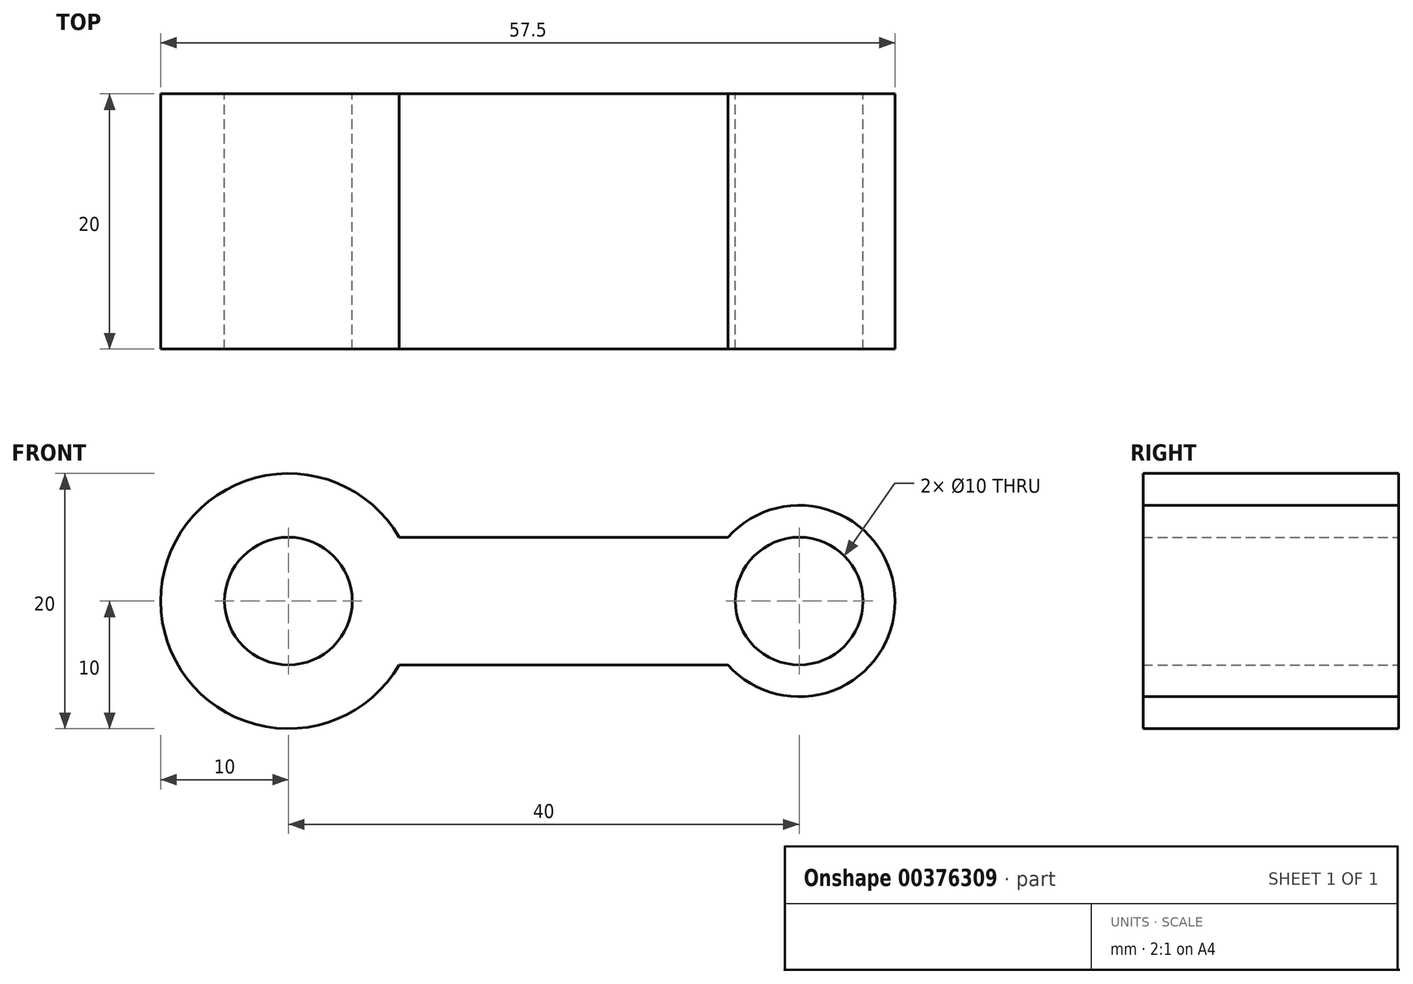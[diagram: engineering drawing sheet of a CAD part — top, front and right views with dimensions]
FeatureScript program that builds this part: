
annotation { "Feature Type Name" : "Feature", "Feature Type Description" : "" }
export const myFeature = defineFeature(function(context is Context, id is Id, definition is map)
    precondition{}
    {
        {
            var Q0;
            Q0=qCreatedBy(makeId("Front.planeOp"),FACE);
            var sketch = newSketch(context, id + "F0", { "sketchPlane" : qUnion([Q0])});
            skCircle(sketch, "E0", {"center": v(0, 0) * mm, "radius": 10 * mm});
            skCircle(sketch, "E1", {"center": v(40, 0) * mm, "radius": 7.5 * mm});
            skLineSegment(sketch, "E2", {"start": v(0, 0) * mm, "end": v(40, 0) * mm, "construction": true});
            skLineSegment(sketch, "E3", {"start": v(8.66, 5) * mm, "end": v(34.4, 5) * mm});
            skLineSegment(sketch, "E4.MirrorCS", {"start": v(8.66, -5) * mm, "end": v(34.4, -5) * mm});
            skCircle(sketch, "E5", {"center": v(0, 0) * mm, "radius": 5 * mm});
            skCircle(sketch, "E6", {"center": v(40, 0) * mm, "radius": 5 * mm});
            skSolve(sketch);
        }
        {
            var Q0;
            {var subQ0=sQuery(id+"F0.wireOp",EDGE,"E3");Q0=makeQuery(id+"F0.imprint","IMPRINT",FACE,{"disambiguationData":[TD([[makeQuery(id+"F0.imprint","IMPRINT",EDGE,{"derivedFrom":subQ0}),-1.0]])]});}
            var Q1;
            Q1=makeQuery(id+"F0.imprint","IMPRINT",FACE,{"disambiguationData":[TD([[makeQuery(id+"F0.imprint","IMPRINT",EDGE,{"derivedFrom":sQuery(id+"F0.wireOp",EDGE,"E6")}),-1.0]])]});
            var Q2;
            Q2=makeQuery(id+"F0.imprint","IMPRINT",FACE,{"disambiguationData":[TD([[makeQuery(id+"F0.imprint","IMPRINT",EDGE,{"derivedFrom":sQuery(id+"F0.wireOp",EDGE,"E5")}),-1.0]])]});
            extrude(context, id + "F1", {"entities" : qUnion([Q0, Q1, Q2]), "endBound" : BoundingType.SYMMETRIC, "depth" : 20 * mm});
        }
    });
